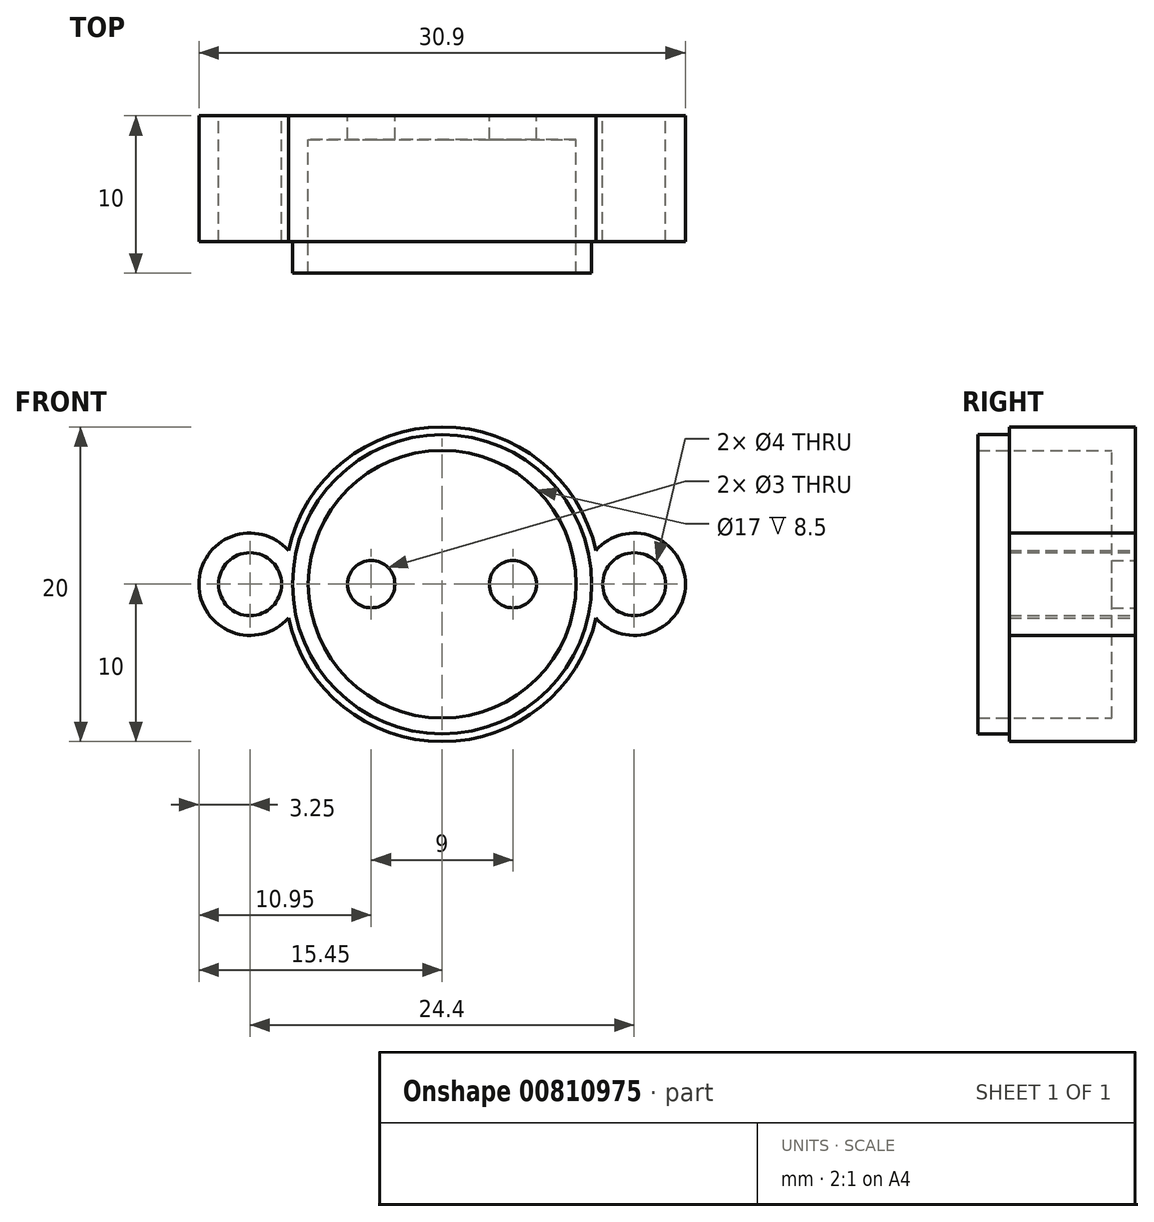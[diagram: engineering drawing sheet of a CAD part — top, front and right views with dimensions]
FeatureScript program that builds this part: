
annotation { "Feature Type Name" : "Feature", "Feature Type Description" : "" }
export const myFeature = defineFeature(function(context is Context, id is Id, definition is map)
    precondition{}
    {
        {
            var Q0;
            Q0=qCreatedBy(makeId("Front.planeOp"),FACE);
            var sketch = newSketch(context, id + "F0", { "sketchPlane" : qUnion([Q0])});
            skCircle(sketch, "E0", {"center": v(0, 0) * mm, "radius": 8.5 * mm});
            skCircle(sketch, "E1", {"center": v(0, 0) * mm, "radius": 10 * mm});
            skCircle(sketch, "E2", {"center": v(-4.5, 0) * mm, "radius": 1.5 * mm});
            skCircle(sketch, "E3", {"center": v(4.5, 0) * mm, "radius": 1.5 * mm});
            skCircle(sketch, "E4", {"center": v(0, 0) * mm, "radius": 9.5 * mm});
            skCircle(sketch, "E5", {"center": v(12.2, 0) * mm, "radius": 3.25 * mm});
            skCircle(sketch, "E6", {"center": v(-12.2, 0) * mm, "radius": 3.25 * mm});
            skCircle(sketch, "E7", {"center": v(-12.2, 0) * mm, "radius": 2 * mm});
            skCircle(sketch, "E8", {"center": v(12.2, 0) * mm, "radius": 2 * mm});
            skSolve(sketch);
        }
        {
            var Q0;
            Q0=makeQuery(id+"F0.imprint","IMPRINT",FACE,{"disambiguationData":[TD([[makeQuery(id+"F0.imprint","IMPRINT",EDGE,{"derivedFrom":sQuery(id+"F0.wireOp",EDGE,"E0")}),-1.0]])]});
            extrude(context, id + "F1", {"entities" : qUnion([Q0]), "depth" : 10 * mm, "offsetDistance" : 25 * mm});
        }
        {
            var Q0;
            Q0 = qSketchRegion(id + "F0", true);
            extrude(context, id + "F2", {"entities" : qUnion([Q0]), "operationType" : NewBodyOperationType.ADD, "depth" : 8 * mm, "offsetDistance" : 25 * mm});
        }
        {
            var Q0;
            Q0=makeQuery(id+"F0.imprint","IMPRINT",FACE,{"disambiguationData":[TD([[makeQuery(id+"F0.imprint","IMPRINT",EDGE,{"derivedFrom":sQuery(id+"F0.wireOp",EDGE,"E0")}),1.0]])]});
            extrude(context, id + "F3", {"entities" : qUnion([Q0]), "operationType" : NewBodyOperationType.ADD, "depth" : 1.5 * mm, "offsetDistance" : 25 * mm});
        }
        {
            var Q0;
            {var subQ0=sQuery(id+"F0.wireOp",EDGE,"E5");var subQ1=sQuery(id+"F0.wireOp",EDGE,"E4");var subQ2=makeQuery(id+"F0.imprint","INTERSECT",VERTEX,{"disambiguationData":[OD(0.0)],"derivedFrom":[subQ1,subQ0]});Q0=makeQuery(id+"F0.imprint","IMPRINT",FACE,{"disambiguationData":[TD([[makeQuery(id+"F0.imprint","IMPRINT",EDGE,{"disambiguationData":[TD([[subQ2,1.0]])],"derivedFrom":subQ1}),1.0]])]});}
            var Q1;
            {var subQ0=sQuery(id+"F0.wireOp",EDGE,"E6");var subQ1=sQuery(id+"F0.wireOp",EDGE,"E4");var subQ2=makeQuery(id+"F0.imprint","INTERSECT",VERTEX,{"disambiguationData":[OD(0.0)],"derivedFrom":[subQ1,subQ0]});Q1=makeQuery(id+"F0.imprint","IMPRINT",FACE,{"disambiguationData":[TD([[makeQuery(id+"F0.imprint","IMPRINT",EDGE,{"disambiguationData":[TD([[subQ2,-1.0]])],"derivedFrom":subQ1}),1.0]])]});}
            extrude(context, id + "F4", {"entities" : qUnion([Q0, Q1]), "operationType" : NewBodyOperationType.ADD, "depth" : 10 * mm, "offsetDistance" : 25 * mm});
        }
    });
